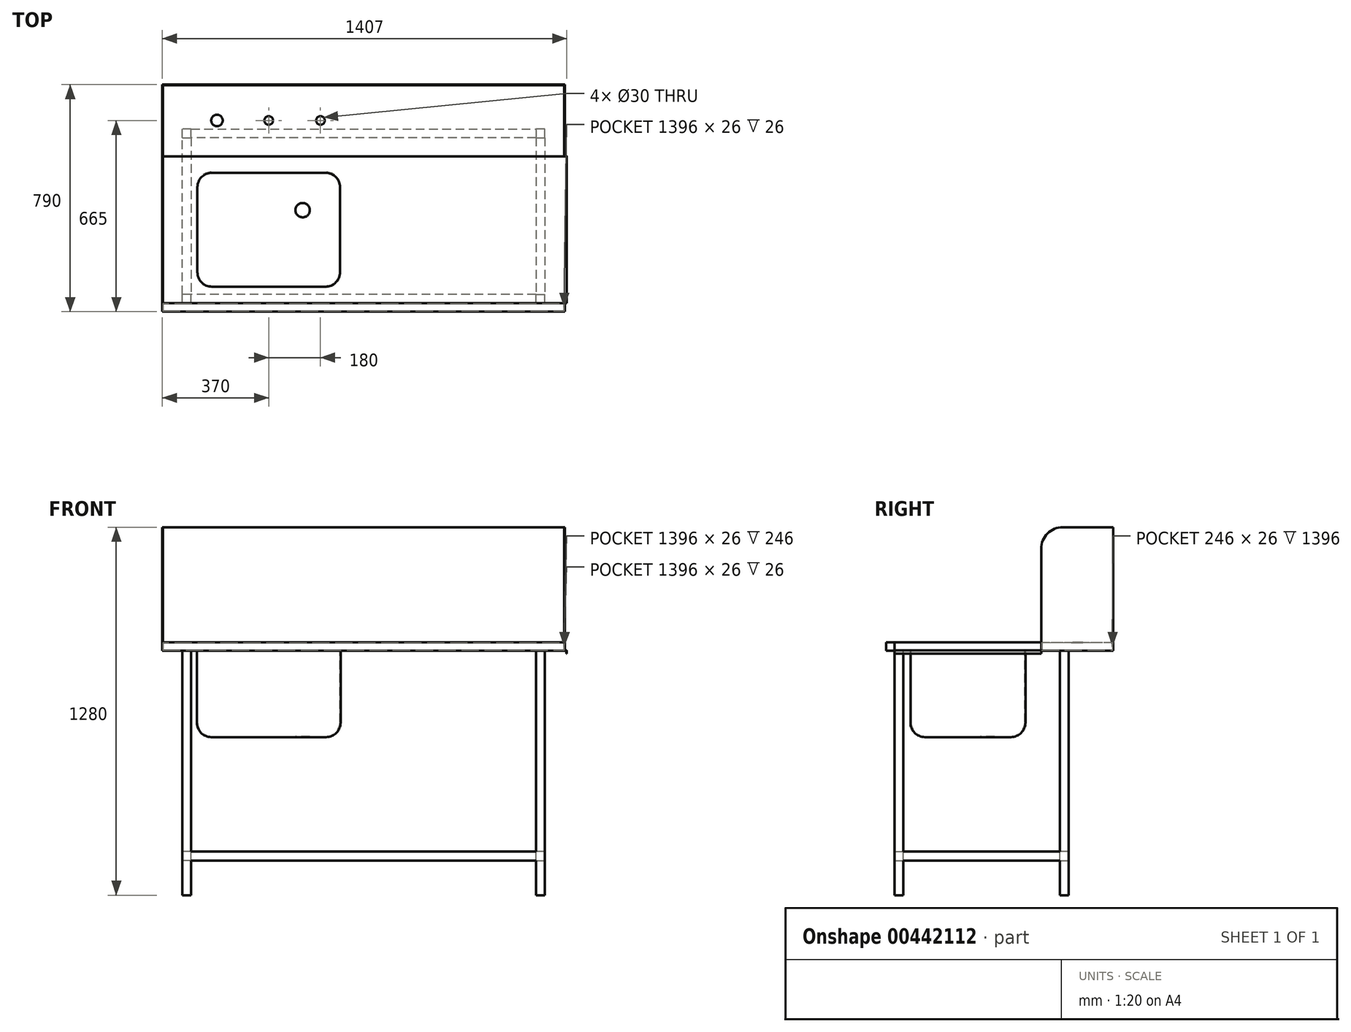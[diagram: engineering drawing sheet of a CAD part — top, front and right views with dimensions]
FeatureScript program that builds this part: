
annotation { "Feature Type Name" : "Feature", "Feature Type Description" : "" }
export const myFeature = defineFeature(function(context is Context, id is Id, definition is map)
    precondition{}
    {
        {
            var Q0;
            Q0=qCreatedBy(makeId("Top.planeOp"),FACE);
            var sketch = newSketch(context, id + "F0", { "sketchPlane" : qUnion([Q0])});
            skLineSegment(sketch, "E0", {"start": v(0, 0) * mm, "end": v(1400, 0) * mm});
            skLineSegment(sketch, "E1", {"start": v(1400, 0) * mm, "end": v(1400, 790) * mm});
            skLineSegment(sketch, "E2", {"start": v(1400, 790) * mm, "end": v(0, 790) * mm});
            skLineSegment(sketch, "E3", {"start": v(0, 790) * mm, "end": v(0, 0) * mm});
            skPoint(sketch, "E4.orphan", {"position": v(0, 690) * mm});
            skSolve(sketch);
        }
        {
            var Q0;
            Q0=qSketchRegion(id+"F0",true);
            extrude(context, id + "F1", {"entities" : qUnion([Q0]), "depth" : 30 * mm});
        }
        {
            var Q0;
            Q0=makeQuery(id+"F1.opExtrude","CAP_FACE",FACE,{"disambiguationData":[OSD([sQuery(id+"F0.wireOp",EDGE,"E0"),sQuery(id+"F0.wireOp",EDGE,"E1"),sQuery(id+"F0.wireOp",EDGE,"E2"),sQuery(id+"F0.wireOp",EDGE,"iw2otP9S-IO86-Xb9D-tqfB-Dh7aYlcr44ko"),sQuery(id+"F0.wireOp",EDGE,"mcYt9Q74-vii6-4R0c-I0xH-BBebaRFYIFW1"),sQuery(id+"F0.wireOp",EDGE,"E3")])],"isStart":false});
            var sketch = newSketch(context, id + "F2", { "sketchPlane" : qUnion([Q0])});
            skLineSegment(sketch, "E5.bottom", {"start": v(2, 30) * mm, "end": v(1400, 30) * mm});
            skLineSegment(sketch, "E5.top", {"start": v(2, 540) * mm, "end": v(1400, 540) * mm});
            skLineSegment(sketch, "E5.left", {"start": v(2, 30) * mm, "end": v(2, 540) * mm});
            skLineSegment(sketch, "E5.right", {"start": v(1400, 30) * mm, "end": v(1400, 540) * mm});
            skSolve(sketch);
        }
        {
            var Q0;
            Q0=qSketchRegion(id+"F2",true);
            extrude(context, id + "F3", {"entities" : qUnion([Q0]), "operationType" : NewBodyOperationType.REMOVE, "oppositeDirection" : true, "depth" : 28 * mm});
        }
        {
            var Q0;
            Q0=makeQuery(id+"F1.opExtrude","CAP_FACE",FACE,{"disambiguationData":[OSD([sQuery(id+"F0.wireOp",EDGE,"E0"),sQuery(id+"F0.wireOp",EDGE,"E1"),sQuery(id+"F0.wireOp",EDGE,"E2"),sQuery(id+"F0.wireOp",EDGE,"iw2otP9S-IO86-Xb9D-tqfB-Dh7aYlcr44ko"),sQuery(id+"F0.wireOp",EDGE,"mcYt9Q74-vii6-4R0c-I0xH-BBebaRFYIFW1"),sQuery(id+"F0.wireOp",EDGE,"E3")])],"isStart":true});
            var sketch = newSketch(context, id + "F4", { "sketchPlane" : qUnion([Q0])});
            skLineSegment(sketch, "E6.bottom", {"start": v(120, -85) * mm, "end": v(620, -85) * mm});
            skLineSegment(sketch, "E6.top", {"start": v(120, -485) * mm, "end": v(620, -485) * mm});
            skLineSegment(sketch, "E6.left", {"start": v(120, -85) * mm, "end": v(120, -485) * mm});
            skLineSegment(sketch, "E6.right", {"start": v(620, -85) * mm, "end": v(620, -485) * mm});
            skSolve(sketch);
        }
        {
            var Q0;
            Q0=qSketchRegion(id+"F4",true);
            extrude(context, id + "F5", {"entities" : qUnion([Q0]), "operationType" : NewBodyOperationType.ADD, "depth" : 300 * mm});
        }
        {
            var Q0;
            Q0=makeQuery(id+"F3.boolean.opBoolean","COPY",FACE,{"derivedFrom":makeQuery(id+"F3.opExtrude","CAP_FACE",FACE,{"disambiguationData":[OSD([sQuery(id+"F2.wireOp",EDGE,"E5.bottom"),sQuery(id+"F2.wireOp",EDGE,"E5.top"),sQuery(id+"F2.wireOp",EDGE,"E5.left"),sQuery(id+"F2.wireOp",EDGE,"E5.right")])],"isStart":false})});
            shell(context, id + "F6", {"entities" : qUnion([Q0]), "thickness" : 2 * mm});
        }
        {
            var Q0;
            Q0=makeQuery(id+"F6.opShell","OFFSET_EDGE",EDGE,{"disambiguationData":[OSD([sQuery(id+"F4.wireOp",EDGE,"E6.top"),sQuery(id+"F4.wireOp",EDGE,"E6.left")])]});
            var Q1;
            Q1=makeQuery(id+"F6.opShell","OFFSET_EDGE",EDGE,{"disambiguationData":[OSD([sQuery(id+"F4.wireOp",EDGE,"E6.top"),sQuery(id+"F4.wireOp",EDGE,"E6.right")])]});
            var Q2;
            Q2=makeQuery(id+"F6.opShell","OFFSET_EDGE",EDGE,{"disambiguationData":[OSD([sQuery(id+"F4.wireOp",EDGE,"E6.bottom"),sQuery(id+"F4.wireOp",EDGE,"E6.left")])]});
            var Q3;
            Q3=makeQuery(id+"F6.opShell","OFFSET_EDGE",EDGE,{"disambiguationData":[OSD([sQuery(id+"F4.wireOp",EDGE,"E6.bottom"),sQuery(id+"F4.wireOp",EDGE,"E6.right")])]});
            var Q4;
            {var subQ0=sQuery(id+"F4.wireOp",EDGE,"E6.right");Q4=makeQuery(id+"F6.opShell","OFFSET_EDGE",EDGE,{"disambiguationData":[OSD([subQ0]),TDD([makeQuery(id+"F5.opExtrude","CAP_EDGE",EDGE,{"disambiguationData":[OSD([subQ0])],"isStart":false})])]});}
            var Q5;
            {var subQ0=sQuery(id+"F4.wireOp",EDGE,"E6.top");Q5=makeQuery(id+"F6.opShell","OFFSET_EDGE",EDGE,{"disambiguationData":[OSD([subQ0]),TDD([makeQuery(id+"F5.opExtrude","CAP_EDGE",EDGE,{"disambiguationData":[OSD([subQ0])],"isStart":false})])]});}
            var Q6;
            {var subQ0=sQuery(id+"F4.wireOp",EDGE,"E6.left");Q6=makeQuery(id+"F6.opShell","OFFSET_EDGE",EDGE,{"disambiguationData":[OSD([subQ0]),TDD([makeQuery(id+"F5.opExtrude","CAP_EDGE",EDGE,{"disambiguationData":[OSD([subQ0])],"isStart":false})])]});}
            var Q7;
            {var subQ0=sQuery(id+"F4.wireOp",EDGE,"E6.bottom");Q7=makeQuery(id+"F6.opShell","OFFSET_EDGE",EDGE,{"disambiguationData":[OSD([subQ0]),TDD([makeQuery(id+"F5.opExtrude","CAP_EDGE",EDGE,{"disambiguationData":[OSD([subQ0])],"isStart":false})])]});}
            var Q8;
            Q8=makeQuery(id+"F5.opExtrude","SWEPT_EDGE",EDGE,{"disambiguationData":[OSD([sQuery(id+"F4.wireOp",EDGE,"E6.bottom"),sQuery(id+"F4.wireOp",EDGE,"E6.left")])]});
            var Q9;
            Q9=makeQuery(id+"F5.opExtrude","CAP_EDGE",EDGE,{"disambiguationData":[OSD([sQuery(id+"F4.wireOp",EDGE,"E6.bottom")])],"isStart":false});
            var Q10;
            Q10=makeQuery(id+"F5.opExtrude","SWEPT_EDGE",EDGE,{"disambiguationData":[OSD([sQuery(id+"F4.wireOp",EDGE,"E6.bottom"),sQuery(id+"F4.wireOp",EDGE,"E6.right")])]});
            var Q11;
            Q11=makeQuery(id+"F5.opExtrude","CAP_EDGE",EDGE,{"disambiguationData":[OSD([sQuery(id+"F4.wireOp",EDGE,"E6.right")])],"isStart":false});
            var Q12;
            Q12=makeQuery(id+"F5.opExtrude","SWEPT_EDGE",EDGE,{"disambiguationData":[OSD([sQuery(id+"F4.wireOp",EDGE,"E6.top"),sQuery(id+"F4.wireOp",EDGE,"E6.right")])]});
            var Q13;
            Q13=makeQuery(id+"F5.opExtrude","CAP_EDGE",EDGE,{"disambiguationData":[OSD([sQuery(id+"F4.wireOp",EDGE,"E6.top")])],"isStart":false});
            var Q14;
            Q14=makeQuery(id+"F5.opExtrude","SWEPT_EDGE",EDGE,{"disambiguationData":[OSD([sQuery(id+"F4.wireOp",EDGE,"E6.top"),sQuery(id+"F4.wireOp",EDGE,"E6.left")])]});
            var Q15;
            Q15=makeQuery(id+"F5.opExtrude","CAP_EDGE",EDGE,{"disambiguationData":[OSD([sQuery(id+"F4.wireOp",EDGE,"E6.left")])],"isStart":false});
            fillet(context, id + "F7", {"entities" : qUnion([Q0, Q1, Q2, Q3, Q4, Q5, Q6, Q7, Q8, Q9, Q10, Q11, Q12, Q13, Q14, Q15]), "radius" : 50 * mm, "tangentPropagation" : true, "allowEdgeOverflow" : false});
        }
        {
            var Q0;
            Q0=makeQuery(id+"F6.opShell","OFFSET_FACE",FACE,{"disambiguationData":[OSD([sQuery(id+"F4.wireOp",EDGE,"E6.bottom"),sQuery(id+"F4.wireOp",EDGE,"E6.top"),sQuery(id+"F4.wireOp",EDGE,"E6.left"),sQuery(id+"F4.wireOp",EDGE,"E6.right")])]});
            var sketch = newSketch(context, id + "F8", { "sketchPlane" : qUnion([Q0])});
            skCircle(sketch, "E7", {"center": v(488, 353) * mm, "radius": 25 * mm});
            skSolve(sketch);
        }
        {
            var Q0;
            Q0=qSketchRegion(id+"F8",true);
            extrude(context, id + "F9", {"entities" : qUnion([Q0]), "operationType" : NewBodyOperationType.REMOVE, "endBound" : BoundingType.UP_TO_NEXT, "oppositeDirection" : true, "depth" : 25 * mm});
        }
        {
            var Q0;
            Q0=makeQuery(id+"F1.opExtrude","CAP_FACE",FACE,{"disambiguationData":[OSD([sQuery(id+"F0.wireOp",EDGE,"E0"),sQuery(id+"F0.wireOp",EDGE,"E1"),sQuery(id+"F0.wireOp",EDGE,"E2"),sQuery(id+"F0.wireOp",EDGE,"iw2otP9S-IO86-Xb9D-tqfB-Dh7aYlcr44ko"),sQuery(id+"F0.wireOp",EDGE,"mcYt9Q74-vii6-4R0c-I0xH-BBebaRFYIFW1"),sQuery(id+"F0.wireOp",EDGE,"E3")])],"isStart":false});
            var sketch = newSketch(context, id + "F10", { "sketchPlane" : qUnion([Q0])});
            skCircle(sketch, "E8", {"center": v(550, 665) * mm, "radius": 15 * mm});
            skCircle(sketch, "E9", {"center": v(370, 665) * mm, "radius": 15 * mm});
            skCircle(sketch, "E10", {"center": v(190, 665) * mm, "radius": 20 * mm});
            skSolve(sketch);
        }
        {
            var Q0;
            Q0=qSketchRegion(id+"F10",true);
            var Q1;
            Q1=makeQuery(id+"F1.opExtrude","CAP_FACE",FACE,{"disambiguationData":[OSD([sQuery(id+"F0.wireOp",EDGE,"E0"),sQuery(id+"F0.wireOp",EDGE,"E1"),sQuery(id+"F0.wireOp",EDGE,"E2"),sQuery(id+"F0.wireOp",EDGE,"iw2otP9S-IO86-Xb9D-tqfB-Dh7aYlcr44ko"),sQuery(id+"F0.wireOp",EDGE,"mcYt9Q74-vii6-4R0c-I0xH-BBebaRFYIFW1"),sQuery(id+"F0.wireOp",EDGE,"E3")])],"isStart":true});
            extrude(context, id + "F11", {"entities" : qUnion([Q0]), "operationType" : NewBodyOperationType.REMOVE, "endBound" : BoundingType.UP_TO_SURFACE, "oppositeDirection" : true, "endBoundEntityFace" : qUnion([Q1]), "depth" : 25 * mm});
        }
        {
            var Q0;
            Q0=makeQuery(id+"F1.opExtrude","SWEPT_FACE",FACE,{"disambiguationData":[OSD([sQuery(id+"F0.wireOp",EDGE,"E1")])]});
            var sketch = newSketch(context, id + "F12", { "sketchPlane" : qUnion([Q0])});
            skLineSegment(sketch, "E11.bottom", {"start": v(30, 2) * mm, "end": v(540, 2) * mm});
            skLineSegment(sketch, "E11.top", {"start": v(30, 0) * mm, "end": v(540, 0) * mm});
            skLineSegment(sketch, "E11.left", {"start": v(30, 2) * mm, "end": v(30, 0) * mm});
            skLineSegment(sketch, "E11.right", {"start": v(540, 2) * mm, "end": v(540, 0) * mm});
            skSolve(sketch);
        }
        {
            var Q0;
            Q0=qSketchRegion(id+"F12",true);
            extrude(context, id + "F13", {"entities" : qUnion([Q0]), "operationType" : NewBodyOperationType.ADD, "depth" : 5 * mm});
        }
        {
            var Q0;
            Q0=makeQuery(id+"F13.opExtrude","CAP_FACE",FACE,{"disambiguationData":[OSD([sQuery(id+"F12.wireOp",EDGE,"E11.bottom"),sQuery(id+"F12.wireOp",EDGE,"E11.top"),sQuery(id+"F12.wireOp",EDGE,"E11.left"),sQuery(id+"F12.wireOp",EDGE,"E11.right")])],"isStart":false});
            var sketch = newSketch(context, id + "F14", { "sketchPlane" : qUnion([Q0])});
            skSolve(sketch);
        }
        {
            var Q0;
            Q0=makeQuery(id+"F14.imprint","IMPRINT",FACE,{"disambiguationData":[TD([[makeQuery(id+"F14.imprint","IMPRINT",EDGE,{"derivedFrom":makeQuery(id+"F13.opExtrude","CAP_EDGE",EDGE,{"disambiguationData":[OSD([sQuery(id+"F12.wireOp",EDGE,"E11.bottom")])],"isStart":false})}),-1.0]])]});
            var Q1;
            Q1=makeQuery(id+"F13.opExtrude","CAP_EDGE",EDGE,{"disambiguationData":[OSD([sQuery(id+"F12.wireOp",EDGE,"E11.top")])],"isStart":false});
            revolve(context, id + "F15", {"operationType" : NewBodyOperationType.ADD, "entities" : qUnion([Q0]), "axis" : qUnion([Q1]), "revolveType" : RevolveType.ONE_DIRECTION, "angle" : 90 * degree});
        }
        {
            var Q0;
            {var subQ0=sQuery(id+"F12.wireOp",EDGE,"E11.top");Q0=makeQuery(id+"F15.boolean.opBoolean","MERGE",FACE,{"derivedFrom":[makeQuery(id+"F13.boolean.opBoolean","MERGE",FACE,{"derivedFrom":[makeQuery(id+"F1.opExtrude","CAP_FACE",FACE,{"disambiguationData":[OSD([sQuery(id+"F0.wireOp",EDGE,"E0"),sQuery(id+"F0.wireOp",EDGE,"E1"),sQuery(id+"F0.wireOp",EDGE,"E2"),sQuery(id+"F0.wireOp",EDGE,"iw2otP9S-IO86-Xb9D-tqfB-Dh7aYlcr44ko"),sQuery(id+"F0.wireOp",EDGE,"mcYt9Q74-vii6-4R0c-I0xH-BBebaRFYIFW1"),sQuery(id+"F0.wireOp",EDGE,"E3")])],"isStart":true}),makeQuery(id+"F13.opExtrude","SWEPT_FACE",FACE,{"disambiguationData":[OSD([subQ0])]})]}),makeQuery(id+"F15.opRevolve","CAP_FACE",FACE,{"disambiguationData":[OSD([sQuery(id+"F12.wireOp",EDGE,"E11.bottom"),subQ0,sQuery(id+"F12.wireOp",EDGE,"E11.left"),sQuery(id+"F12.wireOp",EDGE,"E11.right")])],"isStart":false})]});}
            var sketch = newSketch(context, id + "F16", { "sketchPlane" : qUnion([Q0])});
            skLineSegment(sketch, "E12.bottom", {"start": v(1407, -30) * mm, "end": v(1405, -30) * mm});
            skLineSegment(sketch, "E12.top", {"start": v(1407, -540) * mm, "end": v(1405, -540) * mm});
            skLineSegment(sketch, "E12.left", {"start": v(1407, -30) * mm, "end": v(1407, -540) * mm});
            skLineSegment(sketch, "E12.right", {"start": v(1405, -30) * mm, "end": v(1405, -540) * mm});
            skSolve(sketch);
        }
        {
            var Q0;
            Q0=qSketchRegion(id+"F16",true);
            extrude(context, id + "F17", {"entities" : qUnion([Q0]), "operationType" : NewBodyOperationType.ADD, "depth" : 10 * mm});
        }
        {
            var Q0;
            {var subQ0=sQuery(id+"F12.wireOp",EDGE,"E11.top");Q0=makeQuery(id+"F15.boolean.opBoolean","MERGE",FACE,{"derivedFrom":[makeQuery(id+"F13.boolean.opBoolean","MERGE",FACE,{"derivedFrom":[makeQuery(id+"F1.opExtrude","CAP_FACE",FACE,{"disambiguationData":[OSD([sQuery(id+"F0.wireOp",EDGE,"E0"),sQuery(id+"F0.wireOp",EDGE,"E1"),sQuery(id+"F0.wireOp",EDGE,"E2"),sQuery(id+"F0.wireOp",EDGE,"iw2otP9S-IO86-Xb9D-tqfB-Dh7aYlcr44ko"),sQuery(id+"F0.wireOp",EDGE,"mcYt9Q74-vii6-4R0c-I0xH-BBebaRFYIFW1"),sQuery(id+"F0.wireOp",EDGE,"E3")])],"isStart":true}),makeQuery(id+"F13.opExtrude","SWEPT_FACE",FACE,{"disambiguationData":[OSD([subQ0])]})]}),makeQuery(id+"F15.opRevolve","CAP_FACE",FACE,{"disambiguationData":[OSD([sQuery(id+"F12.wireOp",EDGE,"E11.bottom"),subQ0,sQuery(id+"F12.wireOp",EDGE,"E11.left"),sQuery(id+"F12.wireOp",EDGE,"E11.right")])],"isStart":false})]});}
            var sketch = newSketch(context, id + "F18", { "sketchPlane" : qUnion([Q0])});
            skLineSegment(sketch, "E13.bottom", {"start": v(100, -30) * mm, "end": v(70, -30) * mm});
            skLineSegment(sketch, "E13.top", {"start": v(100, -60) * mm, "end": v(70, -60) * mm});
            skLineSegment(sketch, "E13.left", {"start": v(100, -30) * mm, "end": v(100, -60) * mm});
            skLineSegment(sketch, "E13.right", {"start": v(70, -30) * mm, "end": v(70, -60) * mm});
            skPoint(sketch, "E13.middle", {"position": v(85, -45) * mm});
            skLineSegment(sketch, "E14.bottom", {"start": v(1330, -30) * mm, "end": v(1300, -30) * mm});
            skLineSegment(sketch, "E14.top", {"start": v(1330, -60) * mm, "end": v(1300, -60) * mm});
            skLineSegment(sketch, "E14.left", {"start": v(1330, -30) * mm, "end": v(1330, -60) * mm});
            skLineSegment(sketch, "E14.right", {"start": v(1300, -30) * mm, "end": v(1300, -60) * mm});
            skPoint(sketch, "E14.middle", {"position": v(1315, -45) * mm});
            skPoint(sketch, "E14.middle.positionSnap0", {"position": v(70, -45) * mm});
            skPoint(sketch, "E14.centerSnap0", {"position": v(70, -45) * mm});
            skLineSegment(sketch, "E15.bottom", {"start": v(1330, -605) * mm, "end": v(1300, -605) * mm});
            skLineSegment(sketch, "E15.top", {"start": v(1330, -635) * mm, "end": v(1300, -635) * mm});
            skLineSegment(sketch, "E15.left", {"start": v(1330, -605) * mm, "end": v(1330, -635) * mm});
            skLineSegment(sketch, "E15.right", {"start": v(1300, -605) * mm, "end": v(1300, -635) * mm});
            skPoint(sketch, "E15.middle", {"position": v(1315, -620) * mm});
            skLineSegment(sketch, "E16.bottom", {"start": v(100, -605) * mm, "end": v(70, -605) * mm});
            skLineSegment(sketch, "E16.top", {"start": v(100, -635) * mm, "end": v(70, -635) * mm});
            skLineSegment(sketch, "E16.left", {"start": v(100, -605) * mm, "end": v(100, -635) * mm});
            skLineSegment(sketch, "E16.right", {"start": v(70, -605) * mm, "end": v(70, -635) * mm});
            skPoint(sketch, "E16.middle", {"position": v(85, -620) * mm});
            skPoint(sketch, "E16.middle.positionSnap0", {"position": v(1300, -620) * mm});
            skPoint(sketch, "E16.centerSnap0", {"position": v(1300, -620) * mm});
            skSolve(sketch);
        }
        {
            var Q0;
            Q0=qSketchRegion(id+"F18",true);
            extrude(context, id + "F19", {"entities" : qUnion([Q0]), "operationType" : NewBodyOperationType.ADD, "depth" : 850 * mm});
        }
        {
            var Q0;
            Q0=makeQuery(id+"F19.opExtrude","SWEPT_FACE",FACE,{"disambiguationData":[OSD([sQuery(id+"F18.wireOp",EDGE,"E13.left")])]});
            var sketch = newSketch(context, id + "F20", { "sketchPlane" : qUnion([Q0])});
            skLineSegment(sketch, "E17.bottom", {"start": v(30, -730) * mm, "end": v(60, -730) * mm});
            skLineSegment(sketch, "E17.top", {"start": v(30, -700) * mm, "end": v(60, -700) * mm});
            skLineSegment(sketch, "E17.left", {"start": v(30, -730) * mm, "end": v(30, -700) * mm});
            skLineSegment(sketch, "E17.right", {"start": v(60, -730) * mm, "end": v(60, -700) * mm});
            skLineSegment(sketch, "E18.bottom", {"start": v(605, -700) * mm, "end": v(635, -700) * mm});
            skLineSegment(sketch, "E18.top", {"start": v(605, -730) * mm, "end": v(635, -730) * mm});
            skLineSegment(sketch, "E18.left", {"start": v(605, -700) * mm, "end": v(605, -730) * mm});
            skLineSegment(sketch, "E18.right", {"start": v(635, -700) * mm, "end": v(635, -730) * mm});
            skSolve(sketch);
        }
        {
            var Q0;
            Q0=qSketchRegion(id+"F20",true);
            extrude(context, id + "F21", {"entities" : qUnion([Q0]), "operationType" : NewBodyOperationType.ADD, "endBound" : BoundingType.UP_TO_NEXT, "depth" : 25 * mm});
        }
        {
            var Q0;
            Q0=makeQuery(id+"F21.boolean.opBoolean","MERGE",FACE,{"derivedFrom":[makeQuery(id+"F19.opExtrude","SWEPT_FACE",FACE,{"disambiguationData":[OSD([sQuery(id+"F18.wireOp",EDGE,"E13.top")])]}),makeQuery(id+"F19.opExtrude","SWEPT_FACE",FACE,{"disambiguationData":[OSD([sQuery(id+"F18.wireOp",EDGE,"E14.top")])]}),makeQuery(id+"F21.opExtrude","SWEPT_FACE",FACE,{"disambiguationData":[OSD([sQuery(id+"F20.wireOp",EDGE,"E17.right")])]})]});
            var sketch = newSketch(context, id + "F22", { "sketchPlane" : qUnion([Q0])});
            skLineSegment(sketch, "E19.bottom", {"start": v(-1300, -730) * mm, "end": v(-1330, -730) * mm});
            skLineSegment(sketch, "E19.top", {"start": v(-1300, -700) * mm, "end": v(-1330, -700) * mm});
            skLineSegment(sketch, "E19.left", {"start": v(-1300, -730) * mm, "end": v(-1300, -700) * mm});
            skLineSegment(sketch, "E19.right", {"start": v(-1330, -730) * mm, "end": v(-1330, -700) * mm});
            skLineSegment(sketch, "E20.bottom", {"start": v(-100, -730) * mm, "end": v(-70, -730) * mm});
            skLineSegment(sketch, "E20.top", {"start": v(-100, -700) * mm, "end": v(-70, -700) * mm});
            skLineSegment(sketch, "E20.left", {"start": v(-100, -730) * mm, "end": v(-100, -700) * mm});
            skLineSegment(sketch, "E20.right", {"start": v(-70, -730) * mm, "end": v(-70, -700) * mm});
            skSolve(sketch);
        }
        {
            var Q0;
            Q0=qSketchRegion(id+"F22",true);
            extrude(context, id + "F23", {"entities" : qUnion([Q0]), "operationType" : NewBodyOperationType.ADD, "endBound" : BoundingType.UP_TO_NEXT, "depth" : 25 * mm});
        }
        {
            var Q0;
            Q0=makeQuery(id+"F21.opExtrude","SWEPT_FACE",FACE,{"disambiguationData":[OSD([sQuery(id+"F20.wireOp",EDGE,"E17.top")])]});
            var sketch = newSketch(context, id + "F24", { "sketchPlane" : qUnion([Q0])});
            skLineSegment(sketch, "E21", {"start": v(100, 30) * mm, "end": v(100, 60) * mm});
            skLineSegment(sketch, "E22", {"start": v(100, 60) * mm, "end": v(70, 60) * mm});
            skLineSegment(sketch, "E23", {"start": v(70, 60) * mm, "end": v(70, 605) * mm});
            skLineSegment(sketch, "E24", {"start": v(70, 605) * mm, "end": v(100, 605) * mm});
            skLineSegment(sketch, "E25", {"start": v(100, 605) * mm, "end": v(100, 635) * mm});
            skLineSegment(sketch, "E26", {"start": v(100, 635) * mm, "end": v(1300, 635) * mm});
            skLineSegment(sketch, "E27", {"start": v(1300, 635) * mm, "end": v(1300, 605) * mm});
            skLineSegment(sketch, "E28", {"start": v(1300, 605) * mm, "end": v(1330, 605) * mm});
            skLineSegment(sketch, "E29", {"start": v(1330, 605) * mm, "end": v(1330, 60) * mm});
            skLineSegment(sketch, "E30", {"start": v(1330, 60) * mm, "end": v(1300, 60) * mm});
            skLineSegment(sketch, "E31", {"start": v(1300, 60) * mm, "end": v(1300, 30) * mm});
            skLineSegment(sketch, "E32", {"start": v(1300, 30) * mm, "end": v(100, 30) * mm});
            skSolve(sketch);
        }
        {
            var Q0;
            Q0=qSketchRegion(id+"F24",true);
            extrude(context, id + "F25", {"entities" : qUnion([Q0]), "operationType" : NewBodyOperationType.ADD, "depth" : 2 * mm});
        }
        {
            var Q0;
            Q0=makeQuery(id+"F1.opExtrude","CAP_FACE",FACE,{"disambiguationData":[OSD([sQuery(id+"F0.wireOp",EDGE,"E0"),sQuery(id+"F0.wireOp",EDGE,"E1"),sQuery(id+"F0.wireOp",EDGE,"E2"),sQuery(id+"F0.wireOp",EDGE,"E3")])],"isStart":false});
            var sketch = newSketch(context, id + "F26", { "sketchPlane" : qUnion([Q0])});
            skLineSegment(sketch, "E33", {"start": v(0, 790) * mm, "end": v(1400, 790) * mm});
            skLineSegment(sketch, "E34", {"start": v(1400, 790) * mm, "end": v(1400, 540) * mm});
            skLineSegment(sketch, "E35", {"start": v(1400, 540) * mm, "end": v(1398, 540) * mm});
            skLineSegment(sketch, "E36", {"start": v(1398, 540) * mm, "end": v(1398, 788) * mm});
            skLineSegment(sketch, "E37", {"start": v(1398, 788) * mm, "end": v(2, 788) * mm});
            skLineSegment(sketch, "E38", {"start": v(2, 788) * mm, "end": v(2, 540) * mm});
            skLineSegment(sketch, "E39", {"start": v(2, 540) * mm, "end": v(0, 540) * mm});
            skLineSegment(sketch, "E40", {"start": v(0, 540) * mm, "end": v(0, 790) * mm});
            skSolve(sketch);
        }
        {
            var Q0;
            Q0 = qSketchRegion(id + "F26", true);
            extrude(context, id + "F27", {"entities" : qUnion([Q0]), "operationType" : NewBodyOperationType.ADD, "depth" : 400 * mm});
        }
        {
            var Q0;
            Q0=makeQuery(id+"F27.opExtrude","CAP_EDGE",EDGE,{"disambiguationData":[OSD([sQuery(id+"F26.wireOp",EDGE,"E39")])],"isStart":false});
            var Q1;
            Q1=makeQuery(id+"F27.opExtrude","CAP_EDGE",EDGE,{"disambiguationData":[OSD([sQuery(id+"F26.wireOp",EDGE,"E35")])],"isStart":false});
            fillet(context, id + "F28", {"entities" : qUnion([Q0, Q1]), "radius" : 75 * mm, "tangentPropagation" : true, "allowEdgeOverflow" : false});
        }
    });
